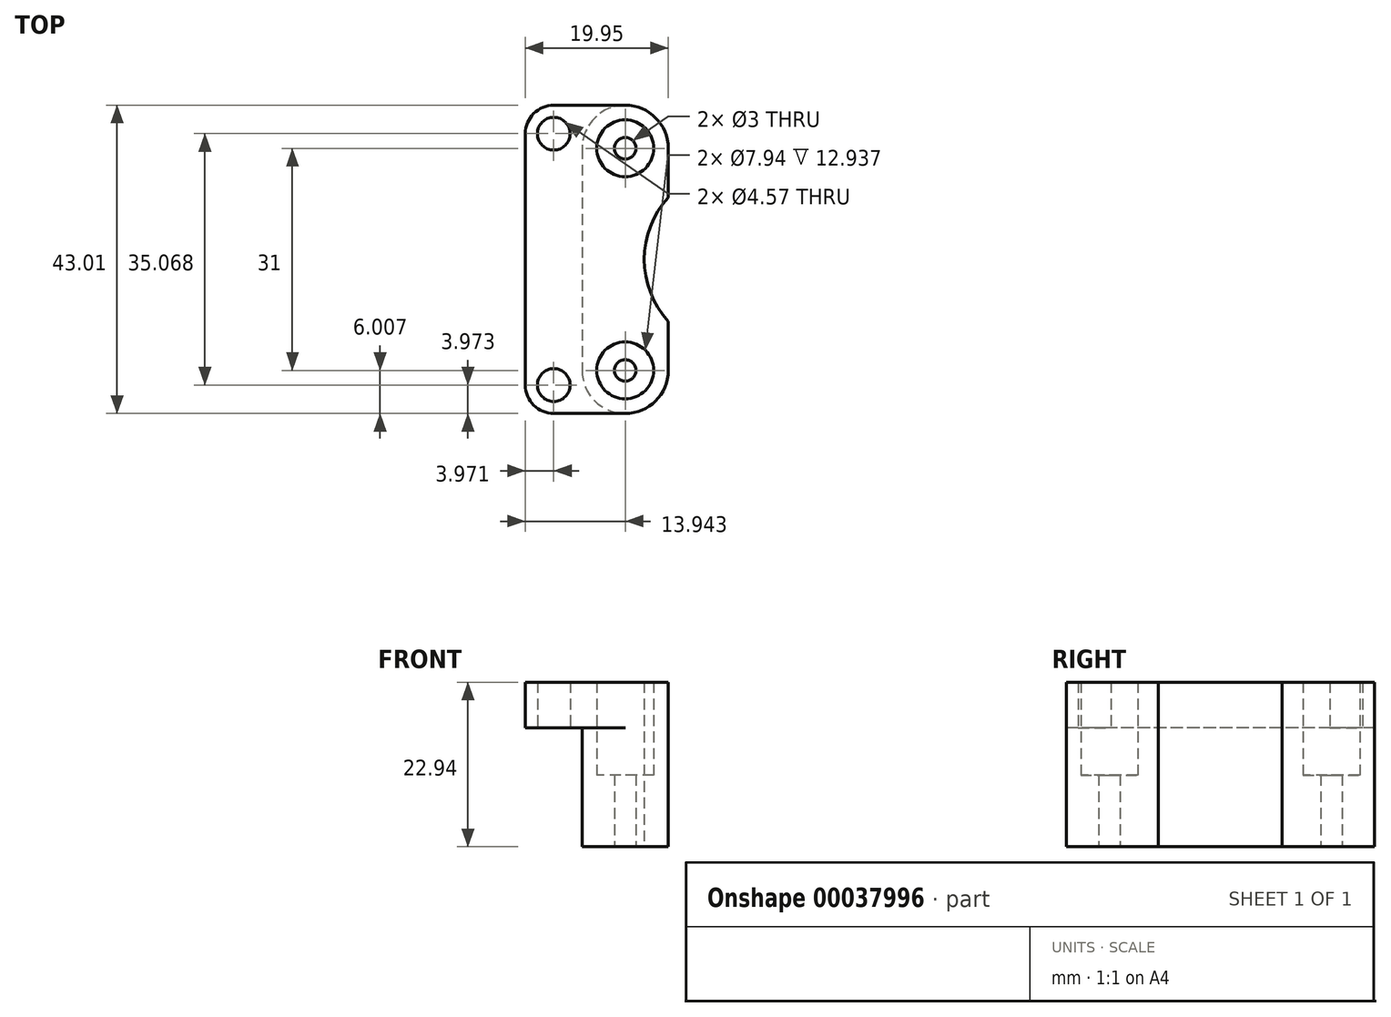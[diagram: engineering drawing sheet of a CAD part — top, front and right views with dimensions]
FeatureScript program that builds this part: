
annotation { "Feature Type Name" : "Feature", "Feature Type Description" : "" }
export const myFeature = defineFeature(function(context is Context, id is Id, definition is map)
    precondition{}
    {
        {
            var Q0;
            Q0=qCreatedBy(makeId("Top.planeOp"),FACE);
            var sketch = newSketch(context, id + "F0", { "sketchPlane" : qUnion([Q0])});
            skLineSegment(sketch, "E0.bottom", {"start": v(0, 0) * mm, "end": v(12, 0) * mm});
            skLineSegment(sketch, "E0.top", {"start": v(0, -43) * mm, "end": v(12, -43) * mm});
            skLineSegment(sketch, "E0.left", {"start": v(0, 0) * mm, "end": v(0, -43) * mm});
            skLineSegment(sketch, "E0.right", {"start": v(12, 0) * mm, "end": v(12, -43) * mm});
            skLineSegment(sketch, "E1", {"start": v(6, 0) * mm, "end": v(6, -12) * mm});
            skLineSegment(sketch, "E2", {"start": v(6, -43) * mm, "end": v(6, -31) * mm});
            skCircle(sketch, "E3", {"center": v(6, -37) * mm, "radius": 1.5 * mm});
            skCircle(sketch, "E4", {"center": v(6, -6) * mm, "radius": 1.5 * mm});
            skSolve(sketch);
        }
        {
            var Q0;
            Q0=qSketchRegion(id+"F0",true);
            extrude(context, id + "F1", {"entities" : qUnion([Q0]), "depth" : 10 * mm});
        }
        {
            var Q0;
            Q0=makeQuery(id+"F1.opExtrude","CAP_FACE",FACE,{"disambiguationData":[OSD([sQuery(id+"F0.wireOp",EDGE,"E0.bottom"),sQuery(id+"F0.wireOp",EDGE,"E0.top"),sQuery(id+"F0.wireOp",EDGE,"E0.left"),sQuery(id+"F0.wireOp",EDGE,"E0.right"),sQuery(id+"F0.wireOp",EDGE,"E3"),sQuery(id+"F0.wireOp",EDGE,"E4")])],"isStart":false});
            var sketch = newSketch(context, id + "F2", { "sketchPlane" : qUnion([Q0])});
            skLineSegment(sketch, "E5.bottom", {"start": v(12, 0) * mm, "end": v(-7.94, 0) * mm});
            skLineSegment(sketch, "E5.top", {"start": v(12, -43) * mm, "end": v(-7.94, -43) * mm});
            skLineSegment(sketch, "E5.left", {"start": v(12, 0) * mm, "end": v(12, -43) * mm});
            skLineSegment(sketch, "E5.right", {"start": v(-7.94, 0) * mm, "end": v(-7.94, -43) * mm});
            skCircle(sketch, "E6", {"center": v(6, -6) * mm, "radius": 3.97 * mm});
            skCircle(sketch, "E7", {"center": v(6, -37) * mm, "radius": 3.97 * mm});
            skLineSegment(sketch, "E8", {"start": v(-3.97, 0) * mm, "end": v(-3.97, -3.97) * mm});
            skLineSegment(sketch, "E9", {"start": v(-3.97, -3.97) * mm, "end": v(-7.94, -3.97) * mm});
            skLineSegment(sketch, "E10", {"start": v(-3.97, -43) * mm, "end": v(-3.97, -39.04) * mm});
            skCircle(sketch, "E11", {"center": v(-3.97, -3.97) * mm, "radius": 2.29 * mm});
            skCircle(sketch, "E12", {"center": v(-3.97, -39.04) * mm, "radius": 2.29 * mm});
            skSolve(sketch);
        }
        {
            var Q0;
            Q0=qSketchRegion(id+"F2",true);
            extrude(context, id + "F3", {"entities" : qUnion([Q0]), "operationType" : NewBodyOperationType.ADD, "depth" : 12.94 * mm});
        }
        {
            var Q0;
            Q0=makeQuery(id+"F3.boolean.opBoolean","MERGE",EDGE,{"derivedFrom":[makeQuery(id+"F1.opExtrude","SWEPT_EDGE",EDGE,{"disambiguationData":[OSD([sQuery(id+"F0.wireOp",EDGE,"E0.bottom"),sQuery(id+"F0.wireOp",EDGE,"E0.right")])]}),makeQuery(id+"F3.opExtrude","SWEPT_EDGE",EDGE,{"disambiguationData":[OSD([sQuery(id+"F2.wireOp",EDGE,"E5.bottom"),sQuery(id+"F2.wireOp",EDGE,"E5.left")])]})]});
            var Q1;
            Q1=makeQuery(id+"F1.opExtrude","SWEPT_EDGE",EDGE,{"disambiguationData":[OSD([sQuery(id+"F0.wireOp",EDGE,"E0.bottom"),sQuery(id+"F0.wireOp",EDGE,"E0.left")])]});
            var Q2;
            Q2=makeQuery(id+"F1.opExtrude","SWEPT_EDGE",EDGE,{"disambiguationData":[OSD([sQuery(id+"F0.wireOp",EDGE,"E0.top"),sQuery(id+"F0.wireOp",EDGE,"E0.left")])]});
            var Q3;
            Q3=makeQuery(id+"F3.boolean.opBoolean","MERGE",EDGE,{"derivedFrom":[makeQuery(id+"F1.opExtrude","SWEPT_EDGE",EDGE,{"disambiguationData":[OSD([sQuery(id+"F0.wireOp",EDGE,"E0.top"),sQuery(id+"F0.wireOp",EDGE,"E0.right")])]}),makeQuery(id+"F3.opExtrude","SWEPT_EDGE",EDGE,{"disambiguationData":[OSD([sQuery(id+"F2.wireOp",EDGE,"E5.top"),sQuery(id+"F2.wireOp",EDGE,"E5.left")])]})]});
            fillet(context, id + "F4", {"entities" : qUnion([Q0, Q1, Q2, Q3]), "radius" : 6 * mm, "tangentPropagation" : true, "allowEdgeOverflow" : false});
        }
        {
            var Q0;
            Q0=makeQuery(id+"F3.opExtrude","SWEPT_EDGE",EDGE,{"disambiguationData":[OSD([sQuery(id+"F2.wireOp",EDGE,"E5.top"),sQuery(id+"F2.wireOp",EDGE,"E5.right")])]});
            var Q1;
            Q1=makeQuery(id+"F3.opExtrude","SWEPT_EDGE",EDGE,{"disambiguationData":[OSD([sQuery(id+"F2.wireOp",EDGE,"E5.bottom"),sQuery(id+"F2.wireOp",EDGE,"E5.right")])]});
            fillet(context, id + "F5", {"entities" : qUnion([Q0, Q1]), "radius" : 3.97 * mm, "tangentPropagation" : true, "allowEdgeOverflow" : false});
        }
        {
            var Q0;
            Q0=makeQuery(id+"F1.opExtrude","CAP_FACE",FACE,{"disambiguationData":[OSD([sQuery(id+"F0.wireOp",EDGE,"E0.bottom"),sQuery(id+"F0.wireOp",EDGE,"E0.top"),sQuery(id+"F0.wireOp",EDGE,"E0.left"),sQuery(id+"F0.wireOp",EDGE,"E0.right"),sQuery(id+"F0.wireOp",EDGE,"E3"),sQuery(id+"F0.wireOp",EDGE,"E4")])],"isStart":true});
            var sketch = newSketch(context, id + "F6", { "sketchPlane" : qUnion([Q0])});
            skLineSegment(sketch, "E13", {"start": v(0, 21.5) * mm, "end": v(21.5, 21.5) * mm});
            skArc(sketch, "E14", {"start": v(12, 30.15) * mm, "mid": v(8.66, 21.5) * mm, "end": v(12, 12.86) * mm});
            skLineSegment(sketch, "E15", {"start": v(12, 30.15) * mm, "end": v(12, 12.86) * mm});
            skSolve(sketch);
        }
        {
            var Q0;
            Q0=qSketchRegion(id+"F6",true);
            var Q1;
            Q1=makeQuery(id+"F3.opExtrude","CAP_FACE",FACE,{"disambiguationData":[OSD([sQuery(id+"F2.wireOp",EDGE,"E5.bottom"),sQuery(id+"F2.wireOp",EDGE,"E5.top"),sQuery(id+"F2.wireOp",EDGE,"E5.left"),sQuery(id+"F2.wireOp",EDGE,"E5.right"),sQuery(id+"F2.wireOp",EDGE,"E6"),sQuery(id+"F2.wireOp",EDGE,"E7"),sQuery(id+"F2.wireOp",EDGE,"E11"),sQuery(id+"F2.wireOp",EDGE,"E12")])],"isStart":false});
            extrude(context, id + "F7", {"entities" : qUnion([Q0]), "operationType" : NewBodyOperationType.REMOVE, "endBound" : BoundingType.UP_TO_SURFACE, "oppositeDirection" : true, "endBoundEntityFace" : qUnion([Q1]), "depth" : 25.4 * mm});
        }
        {
            var Q0;
            Q0=makeQuery(id+"F3.opExtrude","CAP_FACE",FACE,{"disambiguationData":[OSD([sQuery(id+"F2.wireOp",EDGE,"E5.bottom"),sQuery(id+"F2.wireOp",EDGE,"E5.top"),sQuery(id+"F2.wireOp",EDGE,"E5.left"),sQuery(id+"F2.wireOp",EDGE,"E5.right"),sQuery(id+"F2.wireOp",EDGE,"E6"),sQuery(id+"F2.wireOp",EDGE,"E7"),sQuery(id+"F2.wireOp",EDGE,"E11"),sQuery(id+"F2.wireOp",EDGE,"E12")])],"isStart":true});
            extrude(context, id + "F8", {"entities" : qUnion([Q0]), "operationType" : NewBodyOperationType.REMOVE, "oppositeDirection" : true, "depth" : 6.6 * mm});
        }
    });
